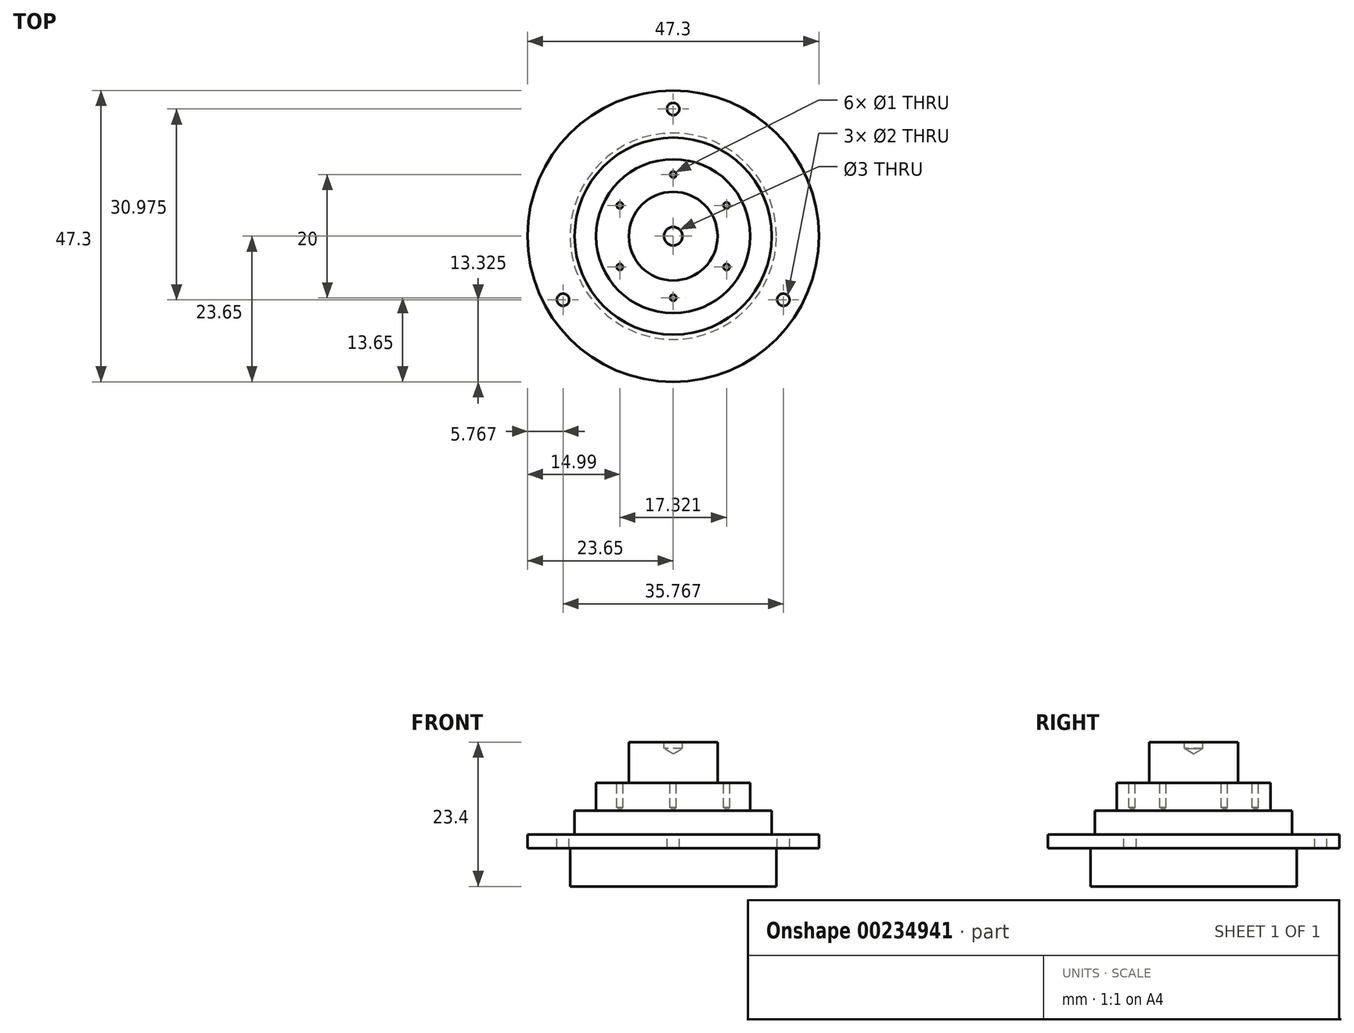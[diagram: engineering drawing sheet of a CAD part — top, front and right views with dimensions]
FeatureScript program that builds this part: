
annotation { "Feature Type Name" : "Feature", "Feature Type Description" : "" }
export const myFeature = defineFeature(function(context is Context, id is Id, definition is map)
    precondition{}
    {
        {
            var Q0;
            Q0=qCreatedBy(makeId("Top.planeOp"),FACE);
            var sketch = newSketch(context, id + "F0", { "sketchPlane" : qUnion([Q0])});
            skCircle(sketch, "E0", {"center": v(0, 0) * mm, "radius": 16.75 * mm});
            skSolve(sketch);
        }
        {
            var Q0;
            Q0 = qSketchRegion(id + "F0", true);
            extrude(context, id + "F1", {"entities" : qUnion([Q0]), "depth" : 6.2 * mm});
        }
        {
            var Q0;
            Q0=makeQuery(id+"F1.opExtrude","CAP_FACE",FACE,{"disambiguationData":[OSD([sQuery(id+"F0.wireOp",EDGE,"E0")])],"isStart":false});
            var sketch = newSketch(context, id + "F2", { "sketchPlane" : qUnion([Q0])});
            skCircle(sketch, "E1", {"center": v(0, 0) * mm, "radius": 23.65 * mm});
            skSolve(sketch);
        }
        {
            var Q0;
            Q0 = qSketchRegion(id + "F2", true);
            extrude(context, id + "F3", {"entities" : qUnion([Q0]), "operationType" : NewBodyOperationType.ADD, "depth" : 2.2 * mm});
        }
        {
            var Q0;
            Q0=makeQuery(id+"F3.opExtrude","CAP_FACE",FACE,{"disambiguationData":[OSD([sQuery(id+"F2.wireOp",EDGE,"E1")])],"isStart":false});
            var sketch = newSketch(context, id + "F4", { "sketchPlane" : qUnion([Q0])});
            skCircle(sketch, "E2", {"center": v(0, 20.65) * mm, "radius": 1 * mm});
            skCircle(sketch, "E3.1.0", {"center": v(17.88, -10.32) * mm, "radius": 1 * mm});
            skCircle(sketch, "E3.2.0", {"center": v(-17.88, -10.33) * mm, "radius": 1 * mm});
            skPoint(sketch, "E3.center", {"position": v(0, 0) * mm});
            skLineSegment(sketch, "E3.anchor1", {"start": v(0, 0) * mm, "end": v(0, 20.65) * mm, "construction": true});
            skLineSegment(sketch, "E3.anchor2", {"start": v(0, 0) * mm, "end": v(-17.88, -10.33) * mm, "construction": true});
            skSolve(sketch);
        }
        {
            var Q0;
            Q0=sQuery(id+"F4.wireOp",VERTEX,"E2.center");
            var Q1;
            Q1=sQuery(id+"F4.wireOp",VERTEX,"E3.1.0.center");
            var Q2;
            Q2=sQuery(id+"F4.wireOp",VERTEX,"E3.2.0.center");
            var Q3;
            Q3=makeQuery(id+"F1.opExtrude","SWEPT_BODY",BODY,{"disambiguationData":[OSD([sQuery(id+"F0.wireOp",EDGE,"E0")])]});
            hole(context, id + "F5", {"style" : HoleStyle.SIMPLE, "endStyle" : HoleEndStyle.THROUGH, "holeDiameter" : 2 * mm, "locations" : qUnion([Q0, Q1, Q2]), "scope" : qUnion([Q3]), "isTappedThrough" : true});
        }
        {
            var Q0;
            Q0=makeQuery(id+"F3.opExtrude","CAP_FACE",FACE,{"disambiguationData":[OSD([sQuery(id+"F2.wireOp",EDGE,"E1")])],"isStart":false});
            var sketch = newSketch(context, id + "F6", { "sketchPlane" : qUnion([Q0])});
            skCircle(sketch, "E4", {"center": v(0, 0) * mm, "radius": 16 * mm});
            skSolve(sketch);
        }
        {
            var Q0;
            Q0 = qSketchRegion(id + "F6", true);
            extrude(context, id + "F7", {"entities" : qUnion([Q0]), "operationType" : NewBodyOperationType.ADD, "depth" : 3.9 * mm});
        }
        {
            var Q0;
            Q0=makeQuery(id+"F7.opExtrude","CAP_FACE",FACE,{"disambiguationData":[OSD([sQuery(id+"F6.wireOp",EDGE,"E4")])],"isStart":false});
            var sketch = newSketch(context, id + "F8", { "sketchPlane" : qUnion([Q0])});
            skCircle(sketch, "E5", {"center": v(0, 0) * mm, "radius": 12.5 * mm});
            skSolve(sketch);
        }
        {
            var Q0;
            Q0 = qSketchRegion(id + "F8", true);
            extrude(context, id + "F9", {"entities" : qUnion([Q0]), "operationType" : NewBodyOperationType.ADD, "depth" : 4.5 * mm});
        }
        {
            var Q0;
            Q0=makeQuery(id+"F9.opExtrude","CAP_FACE",FACE,{"disambiguationData":[OSD([sQuery(id+"F8.wireOp",EDGE,"E5")])],"isStart":false});
            var sketch = newSketch(context, id + "F10", { "sketchPlane" : qUnion([Q0])});
            skPoint(sketch, "E6", {"position": v(0, 10) * mm});
            skPoint(sketch, "E7.1.0", {"position": v(-8.66, 5) * mm});
            skPoint(sketch, "E7.2.0", {"position": v(-8.66, -5) * mm});
            skPoint(sketch, "E7.3.0", {"position": v(0, -10) * mm});
            skPoint(sketch, "E7.4.0", {"position": v(8.66, -5) * mm});
            skPoint(sketch, "E7.5.0", {"position": v(8.66, 5) * mm});
            skPoint(sketch, "E7.center", {"position": v(0, 0) * mm});
            skSolve(sketch);
        }
        {
            var Q0;
            Q0=sQuery(id+"F10.wireOp",VERTEX,"E7.1.0");
            var Q1;
            Q1=sQuery(id+"F10.wireOp",VERTEX,"E6");
            var Q2;
            Q2=sQuery(id+"F10.wireOp",VERTEX,"E7.5.0");
            var Q3;
            Q3=sQuery(id+"F10.wireOp",VERTEX,"E7.4.0");
            var Q4;
            Q4=sQuery(id+"F10.wireOp",VERTEX,"E7.3.0");
            var Q5;
            Q5=sQuery(id+"F10.wireOp",VERTEX,"E7.2.0");
            var Q6;
            Q6=makeQuery(id+"F1.opExtrude","SWEPT_BODY",BODY,{"disambiguationData":[OSD([sQuery(id+"F0.wireOp",EDGE,"E0")])]});
            hole(context, id + "F11", {"style" : HoleStyle.SIMPLE, "endStyle" : HoleEndStyle.BLIND, "holeDiameter" : 1 * mm, "holeDepth" : 4 * mm, "locations" : qUnion([Q0, Q1, Q2, Q3, Q4, Q5]), "scope" : qUnion([Q6])});
        }
        {
            var Q0;
            Q0=makeQuery(id+"F9.opExtrude","CAP_FACE",FACE,{"disambiguationData":[OSD([sQuery(id+"F8.wireOp",EDGE,"E5")])],"isStart":false});
            var sketch = newSketch(context, id + "F12", { "sketchPlane" : qUnion([Q0])});
            skCircle(sketch, "E8", {"center": v(0, 0) * mm, "radius": 7.2 * mm});
            skSolve(sketch);
        }
        {
            var Q0;
            Q0 = qSketchRegion(id + "F12", true);
            extrude(context, id + "F13", {"entities" : qUnion([Q0]), "operationType" : NewBodyOperationType.ADD, "depth" : 6.6 * mm});
        }
        {
            var Q0;
            Q0=makeQuery(id+"F13.opExtrude","CAP_FACE",FACE,{"disambiguationData":[OSD([sQuery(id+"F12.wireOp",EDGE,"E8")])],"isStart":false});
            var sketch = newSketch(context, id + "F14", { "sketchPlane" : qUnion([Q0])});
            skPoint(sketch, "E9", {"position": v(0, 0) * mm});
            skSolve(sketch);
        }
        {
            var Q0;
            Q0=sQuery(id+"F14.wireOp",VERTEX,"E9");
            var Q1;
            Q1=makeQuery(id+"F1.opExtrude","SWEPT_BODY",BODY,{"disambiguationData":[OSD([sQuery(id+"F0.wireOp",EDGE,"E0")])]});
            hole(context, id + "F15", {"style" : HoleStyle.SIMPLE, "endStyle" : HoleEndStyle.BLIND, "holeDiameter" : 3 * mm, "holeDepth" : 1 * mm, "locations" : qUnion([Q0]), "scope" : qUnion([Q1])});
        }
    });
